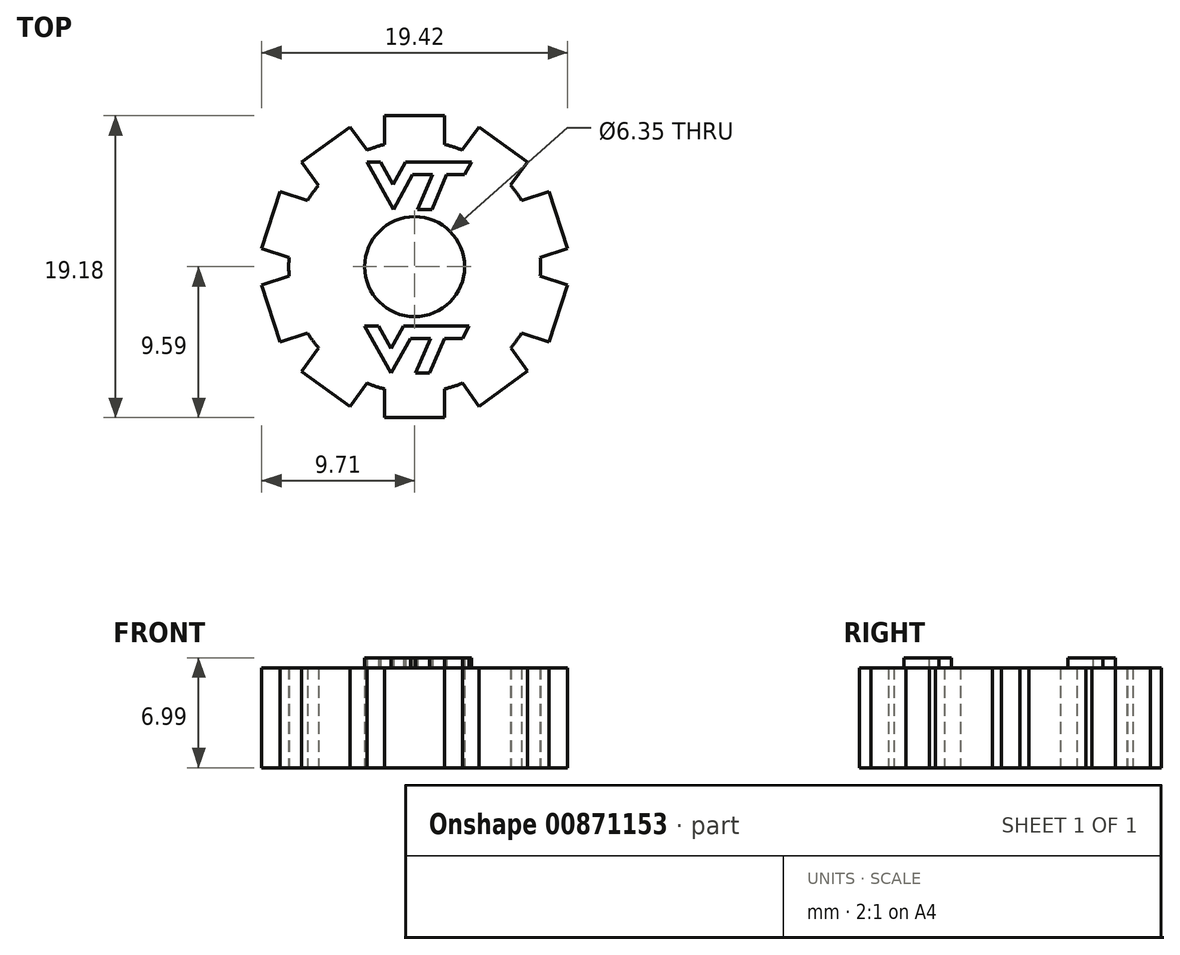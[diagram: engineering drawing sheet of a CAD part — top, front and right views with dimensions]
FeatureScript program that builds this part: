
annotation { "Feature Type Name" : "Feature", "Feature Type Description" : "" }
export const myFeature = defineFeature(function(context is Context, id is Id, definition is map)
    precondition{}
    {
        {
            var Q0;
            Q0=qCreatedBy(makeId("Top.planeOp"),FACE);
            var sketch = newSketch(context, id + "F0", { "sketchPlane" : qUnion([Q0])});
            skPoint(sketch, "E0.center", {"position": v(0, 0) * mm});
            skCircle(sketch, "E1", {"center": v(0, 0) * mm, "radius": 3.18 * mm});
            skArc(sketch, "E2", {"start": v(-6.1, 5.16) * mm, "mid": v(-6.47, 4.7) * mm, "end": v(-6.8, 4.2) * mm});
            skLineSegment(sketch, "E3", {"start": v(1.9, 8) * mm, "end": v(1.9, 9.6) * mm});
            skLineSegment(sketch, "E4", {"start": v(-1.9, 8) * mm, "end": v(-1.9, 9.6) * mm});
            skLineSegment(sketch, "E5", {"start": v(-1.9, 9.6) * mm, "end": v(1.9, 9.6) * mm});
            skLineSegment(sketch, "E6", {"start": v(-1.9, 8) * mm, "end": v(-1.9, 7.77) * mm});
            skLineSegment(sketch, "E7", {"start": v(1.9, 8) * mm, "end": v(1.9, 7.77) * mm});
            skLineSegment(sketch, "E8.1.1", {"start": v(-3.17, 7.59) * mm, "end": v(-4.1, 8.88) * mm});
            skLineSegment(sketch, "E8.1.2", {"start": v(-6.24, 5.35) * mm, "end": v(-7.18, 6.64) * mm});
            skLineSegment(sketch, "E8.1.3", {"start": v(-7.18, 6.64) * mm, "end": v(-4.1, 8.88) * mm});
            skLineSegment(sketch, "E8.1.4", {"start": v(-6.24, 5.35) * mm, "end": v(-6.1, 5.16) * mm});
            skLineSegment(sketch, "E8.1.5", {"start": v(-3.17, 7.59) * mm, "end": v(-3.03, 7.4) * mm});
            skLineSegment(sketch, "E8.2.1", {"start": v(-7.02, 4.28) * mm, "end": v(-8.54, 4.77) * mm});
            skLineSegment(sketch, "E8.2.2", {"start": v(-8.2, 0.66) * mm, "end": v(-9.71, 1.15) * mm});
            skLineSegment(sketch, "E8.2.3", {"start": v(-9.71, 1.15) * mm, "end": v(-8.54, 4.77) * mm});
            skLineSegment(sketch, "E8.2.4", {"start": v(-8.2, 0.66) * mm, "end": v(-7.98, 0.59) * mm});
            skLineSegment(sketch, "E8.2.5", {"start": v(-7.02, 4.28) * mm, "end": v(-6.8, 4.2) * mm});
            skLineSegment(sketch, "E8.3.1", {"start": v(-8.2, -0.67) * mm, "end": v(-9.7, -1.16) * mm});
            skLineSegment(sketch, "E8.3.2", {"start": v(-7.02, -4.28) * mm, "end": v(-8.53, -4.78) * mm});
            skLineSegment(sketch, "E8.3.3", {"start": v(-8.53, -4.78) * mm, "end": v(-9.7, -1.16) * mm});
            skLineSegment(sketch, "E8.3.4", {"start": v(-7.02, -4.28) * mm, "end": v(-6.8, -4.21) * mm});
            skLineSegment(sketch, "E8.3.5", {"start": v(-8.2, -0.67) * mm, "end": v(-7.97, -0.6) * mm});
            skLineSegment(sketch, "E8.4.1", {"start": v(-6.24, -5.35) * mm, "end": v(-7.17, -6.65) * mm});
            skLineSegment(sketch, "E8.4.2", {"start": v(-3.16, -7.6) * mm, "end": v(-4.1, -8.88) * mm});
            skLineSegment(sketch, "E8.4.3", {"start": v(-4.1, -8.88) * mm, "end": v(-7.17, -6.65) * mm});
            skLineSegment(sketch, "E8.4.4", {"start": v(-3.16, -7.6) * mm, "end": v(-3.02, -7.4) * mm});
            skLineSegment(sketch, "E8.4.5", {"start": v(-6.24, -5.35) * mm, "end": v(-6.1, -5.17) * mm});
            skLineSegment(sketch, "E8.5.1", {"start": v(-1.9, -8) * mm, "end": v(-1.9, -9.6) * mm});
            skLineSegment(sketch, "E8.5.2", {"start": v(1.9, -8) * mm, "end": v(1.9, -9.6) * mm});
            skLineSegment(sketch, "E8.5.3", {"start": v(1.9, -9.6) * mm, "end": v(-1.9, -9.6) * mm});
            skLineSegment(sketch, "E8.5.4", {"start": v(1.9, -8) * mm, "end": v(1.9, -7.77) * mm});
            skLineSegment(sketch, "E8.5.5", {"start": v(-1.9, -8) * mm, "end": v(-1.9, -7.77) * mm});
            skLineSegment(sketch, "E8.6.1", {"start": v(3.17, -7.59) * mm, "end": v(4.1, -8.88) * mm});
            skLineSegment(sketch, "E8.6.2", {"start": v(6.24, -5.35) * mm, "end": v(7.18, -6.64) * mm});
            skLineSegment(sketch, "E8.6.3", {"start": v(7.18, -6.64) * mm, "end": v(4.1, -8.88) * mm});
            skLineSegment(sketch, "E8.6.4", {"start": v(6.24, -5.35) * mm, "end": v(6.1, -5.16) * mm});
            skLineSegment(sketch, "E8.6.5", {"start": v(3.17, -7.59) * mm, "end": v(3.03, -7.4) * mm});
            skLineSegment(sketch, "E8.7.1", {"start": v(7.02, -4.28) * mm, "end": v(8.54, -4.77) * mm});
            skLineSegment(sketch, "E8.7.2", {"start": v(8.2, -0.66) * mm, "end": v(9.71, -1.15) * mm});
            skLineSegment(sketch, "E8.7.3", {"start": v(9.71, -1.15) * mm, "end": v(8.54, -4.77) * mm});
            skLineSegment(sketch, "E8.7.4", {"start": v(8.2, -0.66) * mm, "end": v(7.98, -0.59) * mm});
            skLineSegment(sketch, "E8.7.5", {"start": v(7.02, -4.28) * mm, "end": v(6.8, -4.2) * mm});
            skLineSegment(sketch, "E8.8.1", {"start": v(8.2, 0.67) * mm, "end": v(9.7, 1.16) * mm});
            skLineSegment(sketch, "E8.8.2", {"start": v(7.02, 4.28) * mm, "end": v(8.53, 4.78) * mm});
            skLineSegment(sketch, "E8.8.3", {"start": v(8.53, 4.78) * mm, "end": v(9.7, 1.16) * mm});
            skLineSegment(sketch, "E8.8.4", {"start": v(7.02, 4.28) * mm, "end": v(6.8, 4.21) * mm});
            skLineSegment(sketch, "E8.8.5", {"start": v(8.2, 0.67) * mm, "end": v(7.97, 0.6) * mm});
            skLineSegment(sketch, "E8.9.1", {"start": v(6.24, 5.35) * mm, "end": v(7.17, 6.65) * mm});
            skLineSegment(sketch, "E8.9.2", {"start": v(3.16, 7.6) * mm, "end": v(4.1, 8.88) * mm});
            skLineSegment(sketch, "E8.9.3", {"start": v(4.1, 8.88) * mm, "end": v(7.17, 6.65) * mm});
            skLineSegment(sketch, "E8.9.4", {"start": v(3.16, 7.6) * mm, "end": v(3.02, 7.4) * mm});
            skLineSegment(sketch, "E8.9.5", {"start": v(6.24, 5.35) * mm, "end": v(6.1, 5.17) * mm});
            skArc(sketch, "E9.trimOffspring", {"start": v(-1.9, 7.77) * mm, "mid": v(-2.48, 7.6) * mm, "end": v(-3.03, 7.4) * mm});
            skArc(sketch, "E10.trimOffspring", {"start": v(3.02, 7.4) * mm, "mid": v(2.47, 7.6) * mm, "end": v(1.9, 7.77) * mm});
            skArc(sketch, "E11.trimOffspring", {"start": v(6.8, 4.21) * mm, "mid": v(6.47, 4.7) * mm, "end": v(6.1, 5.17) * mm});
            skArc(sketch, "E12.trimOffspring", {"start": v(7.98, -0.59) * mm, "mid": v(8, 0) * mm, "end": v(7.97, 0.6) * mm});
            skArc(sketch, "E13.trimOffspring", {"start": v(6.1, -5.16) * mm, "mid": v(6.47, -4.7) * mm, "end": v(6.8, -4.2) * mm});
            skArc(sketch, "E14.trimOffspring", {"start": v(1.9, -7.77) * mm, "mid": v(2.48, -7.6) * mm, "end": v(3.03, -7.4) * mm});
            skArc(sketch, "E15.trimOffspring", {"start": v(-7.98, 0.59) * mm, "mid": v(-8, 0) * mm, "end": v(-7.97, -0.6) * mm});
            skArc(sketch, "E16.trimOffspring", {"start": v(-6.8, -4.21) * mm, "mid": v(-6.47, -4.7) * mm, "end": v(-6.1, -5.17) * mm});
            skArc(sketch, "E17.trimOffspring", {"start": v(-3.02, -7.4) * mm, "mid": v(-2.47, -7.6) * mm, "end": v(-1.9, -7.77) * mm});
            skSolve(sketch);
        }
        {
            var Q0;
            Q0=makeQuery(id+"F0.imprint","IMPRINT",FACE,{"disambiguationData":[TD([[makeQuery(id+"F0.imprint","IMPRINT",EDGE,{"derivedFrom":sQuery(id+"F0.wireOp",EDGE,"E1")}),-1.0]])]});
            extrude(context, id + "F1", {"entities" : qUnion([Q0]), "depth" : 6.35 * mm, "offsetDistance" : 25.4 * mm});
        }
        {
            var Q0;
            Q0=makeQuery(id+"F1.opExtrude","CAP_FACE",FACE,{"disambiguationData":[OSD([sQuery(id+"F0.wireOp",EDGE,"E1"),sQuery(id+"F0.wireOp",EDGE,"E2"),sQuery(id+"F0.wireOp",EDGE,"E3"),sQuery(id+"F0.wireOp",EDGE,"E4"),sQuery(id+"F0.wireOp",EDGE,"E5"),sQuery(id+"F0.wireOp",EDGE,"E6"),sQuery(id+"F0.wireOp",EDGE,"E7"),sQuery(id+"F0.wireOp",EDGE,"E8.1.1"),sQuery(id+"F0.wireOp",EDGE,"E8.1.2"),sQuery(id+"F0.wireOp",EDGE,"E8.1.3"),sQuery(id+"F0.wireOp",EDGE,"E8.1.4"),sQuery(id+"F0.wireOp",EDGE,"E8.1.5"),sQuery(id+"F0.wireOp",EDGE,"E8.2.1"),sQuery(id+"F0.wireOp",EDGE,"E8.2.2"),sQuery(id+"F0.wireOp",EDGE,"E8.2.3"),sQuery(id+"F0.wireOp",EDGE,"E8.2.4"),sQuery(id+"F0.wireOp",EDGE,"E8.2.5"),sQuery(id+"F0.wireOp",EDGE,"E8.3.1"),sQuery(id+"F0.wireOp",EDGE,"E8.3.2"),sQuery(id+"F0.wireOp",EDGE,"E8.3.3"),sQuery(id+"F0.wireOp",EDGE,"E8.3.4"),sQuery(id+"F0.wireOp",EDGE,"E8.3.5"),sQuery(id+"F0.wireOp",EDGE,"E8.4.1"),sQuery(id+"F0.wireOp",EDGE,"E8.4.2"),sQuery(id+"F0.wireOp",EDGE,"E8.4.3"),sQuery(id+"F0.wireOp",EDGE,"E8.4.4"),sQuery(id+"F0.wireOp",EDGE,"E8.4.5"),sQuery(id+"F0.wireOp",EDGE,"E8.5.1"),sQuery(id+"F0.wireOp",EDGE,"E8.5.2"),sQuery(id+"F0.wireOp",EDGE,"E8.5.3"),sQuery(id+"F0.wireOp",EDGE,"E8.5.4"),sQuery(id+"F0.wireOp",EDGE,"E8.5.5"),sQuery(id+"F0.wireOp",EDGE,"E8.6.1"),sQuery(id+"F0.wireOp",EDGE,"E8.6.2"),sQuery(id+"F0.wireOp",EDGE,"E8.6.3"),sQuery(id+"F0.wireOp",EDGE,"E8.6.4"),sQuery(id+"F0.wireOp",EDGE,"E8.6.5"),sQuery(id+"F0.wireOp",EDGE,"E8.7.1"),sQuery(id+"F0.wireOp",EDGE,"E8.7.2"),sQuery(id+"F0.wireOp",EDGE,"E8.7.3"),sQuery(id+"F0.wireOp",EDGE,"E8.7.4"),sQuery(id+"F0.wireOp",EDGE,"E8.7.5"),sQuery(id+"F0.wireOp",EDGE,"E8.8.1"),sQuery(id+"F0.wireOp",EDGE,"E8.8.2"),sQuery(id+"F0.wireOp",EDGE,"E8.8.3"),sQuery(id+"F0.wireOp",EDGE,"E8.8.4"),sQuery(id+"F0.wireOp",EDGE,"E8.8.5"),sQuery(id+"F0.wireOp",EDGE,"E8.9.1"),sQuery(id+"F0.wireOp",EDGE,"E8.9.2"),sQuery(id+"F0.wireOp",EDGE,"E8.9.3"),sQuery(id+"F0.wireOp",EDGE,"E8.9.4"),sQuery(id+"F0.wireOp",EDGE,"E8.9.5"),sQuery(id+"F0.wireOp",EDGE,"E9.trimOffspring"),sQuery(id+"F0.wireOp",EDGE,"E10.trimOffspring"),sQuery(id+"F0.wireOp",EDGE,"E11.trimOffspring"),sQuery(id+"F0.wireOp",EDGE,"E12.trimOffspring"),sQuery(id+"F0.wireOp",EDGE,"E13.trimOffspring"),sQuery(id+"F0.wireOp",EDGE,"E14.trimOffspring"),sQuery(id+"F0.wireOp",EDGE,"E15.trimOffspring"),sQuery(id+"F0.wireOp",EDGE,"E16.trimOffspring"),sQuery(id+"F0.wireOp",EDGE,"E17.trimOffspring")])],"isStart":false});
            var sketch = newSketch(context, id + "F2", { "sketchPlane" : qUnion([Q0])});
            skLineSegment(sketch, "E18", {"start": v(-3.03, 6.64) * mm, "end": v(-2.15, 6.64) * mm});
            skLineSegment(sketch, "E19", {"start": v(-3.03, 6.64) * mm, "end": v(-1.35, 3.64) * mm});
            skLineSegment(sketch, "E20", {"start": v(-1.35, 3.64) * mm, "end": v(-0.13, 5.85) * mm});
            skLineSegment(sketch, "E21", {"start": v(0.3, 6.64) * mm, "end": v(2.84, 6.64) * mm});
            skLineSegment(sketch, "E22", {"start": v(0.2, 3.64) * mm, "end": v(1.14, 5.86) * mm});
            skPoint(sketch, "E22.endSnap0", {"position": v(1.14, 5.85) * mm});
            skLineSegment(sketch, "E23", {"start": v(-2.15, 6.64) * mm, "end": v(-1.36, 5.22) * mm});
            skLineSegment(sketch, "E24", {"start": v(0.3, 6.64) * mm, "end": v(-0.58, 6.64) * mm});
            skLineSegment(sketch, "E25", {"start": v(-0.58, 6.64) * mm, "end": v(-1.36, 5.22) * mm});
            skLineSegment(sketch, "E26.trimOffspring", {"start": v(-0.58, 6.64) * mm, "end": v(2.84, 6.64) * mm});
            skLineSegment(sketch, "E27", {"start": v(0.2, 3.64) * mm, "end": v(1.1, 3.64) * mm});
            skLineSegment(sketch, "E28", {"start": v(1.1, 3.64) * mm, "end": v(2.03, 5.86) * mm});
            skLineSegment(sketch, "E29.trimOffspring", {"start": v(1.14, 5.85) * mm, "end": v(-0.13, 5.85) * mm});
            skLineSegment(sketch, "E30", {"start": v(2.03, 5.86) * mm, "end": v(3.17, 5.86) * mm});
            skLineSegment(sketch, "E31", {"start": v(3.6, 6.64) * mm, "end": v(2.84, 6.64) * mm});
            skLineSegment(sketch, "E32", {"start": v(3.17, 5.86) * mm, "end": v(3.6, 6.64) * mm});
            skLineSegment(sketch, "E33", {"start": v(-3.17, -3.77) * mm, "end": v(-2.29, -3.77) * mm});
            skLineSegment(sketch, "E34", {"start": v(-3.17, -3.77) * mm, "end": v(-1.5, -6.76) * mm});
            skLineSegment(sketch, "E35", {"start": v(-1.5, -6.76) * mm, "end": v(-0.27, -4.55) * mm});
            skLineSegment(sketch, "E36", {"start": v(0.16, -3.76) * mm, "end": v(2.7, -3.76) * mm});
            skLineSegment(sketch, "E37", {"start": v(0.06, -6.76) * mm, "end": v(1, -4.55) * mm});
            skLineSegment(sketch, "E38", {"start": v(-2.29, -3.77) * mm, "end": v(-1.5, -5.18) * mm});
            skLineSegment(sketch, "E39", {"start": v(0.16, -3.76) * mm, "end": v(-0.71, -3.76) * mm});
            skLineSegment(sketch, "E40", {"start": v(-0.71, -3.76) * mm, "end": v(-1.5, -5.18) * mm});
            skLineSegment(sketch, "E41.trimOffspring", {"start": v(-0.71, -3.76) * mm, "end": v(2.7, -3.76) * mm});
            skLineSegment(sketch, "E42", {"start": v(0.06, -6.76) * mm, "end": v(0.95, -6.76) * mm});
            skLineSegment(sketch, "E43", {"start": v(0.95, -6.76) * mm, "end": v(1.9, -4.55) * mm});
            skLineSegment(sketch, "E44.trimOffspring", {"start": v(1, -4.55) * mm, "end": v(-0.27, -4.55) * mm});
            skLineSegment(sketch, "E45", {"start": v(1.9, -4.55) * mm, "end": v(3.03, -4.55) * mm});
            skLineSegment(sketch, "E46", {"start": v(3.47, -3.76) * mm, "end": v(2.7, -3.76) * mm});
            skLineSegment(sketch, "E47", {"start": v(3.03, -4.55) * mm, "end": v(3.47, -3.76) * mm});
            skSolve(sketch);
        }
        {
            var Q0;
            Q0=makeQuery(id+"F2.imprint","IMPRINT",FACE,{"disambiguationData":[TD([[makeQuery(id+"F2.imprint","IMPRINT",EDGE,{"derivedFrom":sQuery(id+"F2.wireOp",EDGE,"E19")}),1.0]])]});
            var Q1;
            Q1=makeQuery(id+"F2.imprint","IMPRINT",FACE,{"disambiguationData":[TD([[makeQuery(id+"F2.imprint","IMPRINT",EDGE,{"derivedFrom":sQuery(id+"F2.wireOp",EDGE,"E34")}),1.0]])]});
            extrude(context, id + "F3", {"entities" : qUnion([Q0, Q1]), "operationType" : NewBodyOperationType.ADD, "depth" : 0.64 * mm, "offsetDistance" : 25.4 * mm});
        }
    });
